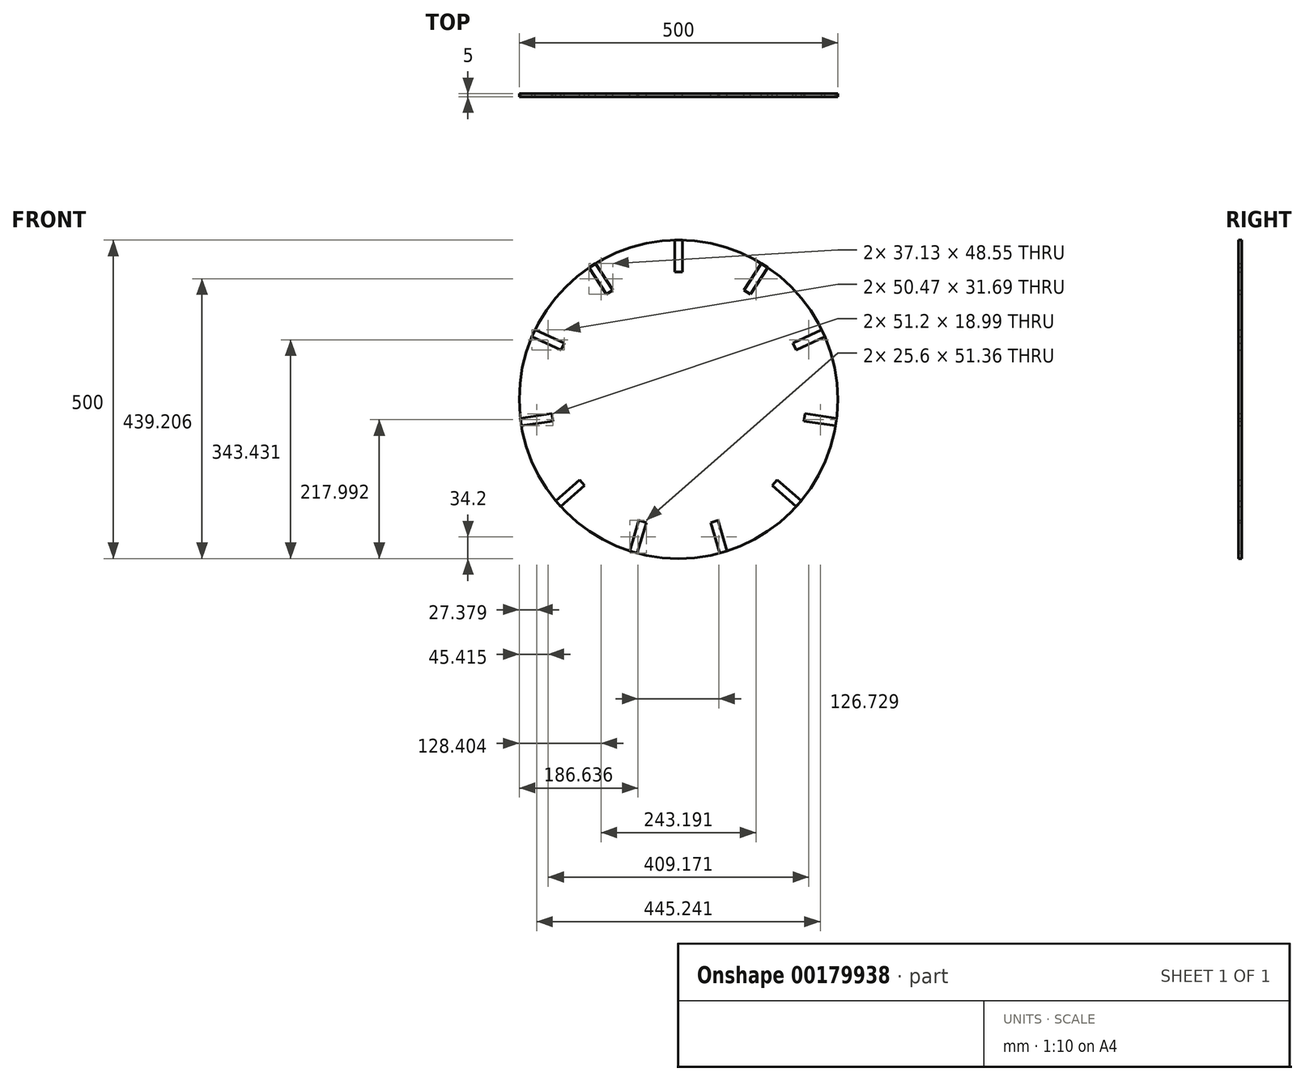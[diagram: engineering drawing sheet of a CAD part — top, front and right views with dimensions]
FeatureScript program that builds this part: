
annotation { "Feature Type Name" : "Feature", "Feature Type Description" : "" }
export const myFeature = defineFeature(function(context is Context, id is Id, definition is map)
    precondition{}
    {
        {
            var Q0;
            Q0=qCreatedBy(makeId("Front.planeOp"),FACE);
            var sketch = newSketch(context, id + "F0", { "sketchPlane" : qUnion([Q0])});
            skCircle(sketch, "E0", {"center": v(0, 0) * mm, "radius": 250 * mm});
            skSolve(sketch);
        }
        {
            var Q0;
            Q0=qCreatedBy(makeId("Front.planeOp"),FACE);
            var sketch = newSketch(context, id + "F1", { "sketchPlane" : qUnion([Q0])});
            skLineSegment(sketch, "E1", {"start": v(0, 0) * mm, "end": v(0, 250) * mm, "construction": true});
            skCircle(sketch, "E2", {"center": v(0, 0) * mm, "radius": 250 * mm, "construction": true});
            skLineSegment(sketch, "E3", {"start": v(0, 0) * mm, "end": v(26.13, 248.63) * mm, "construction": true});
            skCircle(sketch, "E4", {"center": v(0, 0) * mm, "radius": 200 * mm, "construction": true});
            skLineSegment(sketch, "E5.bottom", {"start": v(-6, 199.9) * mm, "end": v(6, 199.9) * mm});
            skLineSegment(sketch, "E5.top", {"start": v(-6, 249.9) * mm, "end": v(6, 249.9) * mm});
            skLineSegment(sketch, "E5.left", {"start": v(-6, 199.9) * mm, "end": v(-6, 249.9) * mm});
            skLineSegment(sketch, "E5.right", {"start": v(6, 199.9) * mm, "end": v(6, 249.9) * mm});
            skPoint(sketch, "E5.middle", {"position": v(0, 224.9) * mm});
            skSolve(sketch);
        }
        {
            var Q0;
            Q0 = qSketchRegion(id + "F0", true);
            var Q1;
            Q1 = qSketchRegion(id + "F1", true);
            extrude(context, id + "F2", {"entities" : qUnion([Q0, Q1]), "depth" : 5 * mm});
        }
        {
            var Q0;
            Q0=qCreatedBy(makeId("Top.planeOp"),FACE);
            var sketch = newSketch(context, id + "F3", { "sketchPlane" : qUnion([Q0])});
            skLineSegment(sketch, "E6", {"start": v(0, 0) * mm, "end": v(0, 145) * mm, "construction": true});
            skSolve(sketch);
        }
        {
            var Q0;
            Q0=makeQuery(id+"F2.opExtrude","SWEPT_BODY",BODY,{"disambiguationData":[OSD([sQuery(id+"F1.wireOp",EDGE,"E5.bottom"),sQuery(id+"F1.wireOp",EDGE,"E5.top"),sQuery(id+"F1.wireOp",EDGE,"E5.left"),sQuery(id+"F1.wireOp",EDGE,"E5.right")])]});
            var Q1;
            Q1=sQuery(id+"F3.wireOp",EDGE,"E6");
            circularPattern(context, id + "F4", {"operationType" : NewBodyOperationType.REMOVE, "entities" : qUnion([Q0]), "axis" : qUnion([Q1]), "angle" : 360 * degree, "instanceCount" : 11, "equalSpace" : true});
        }
    });
